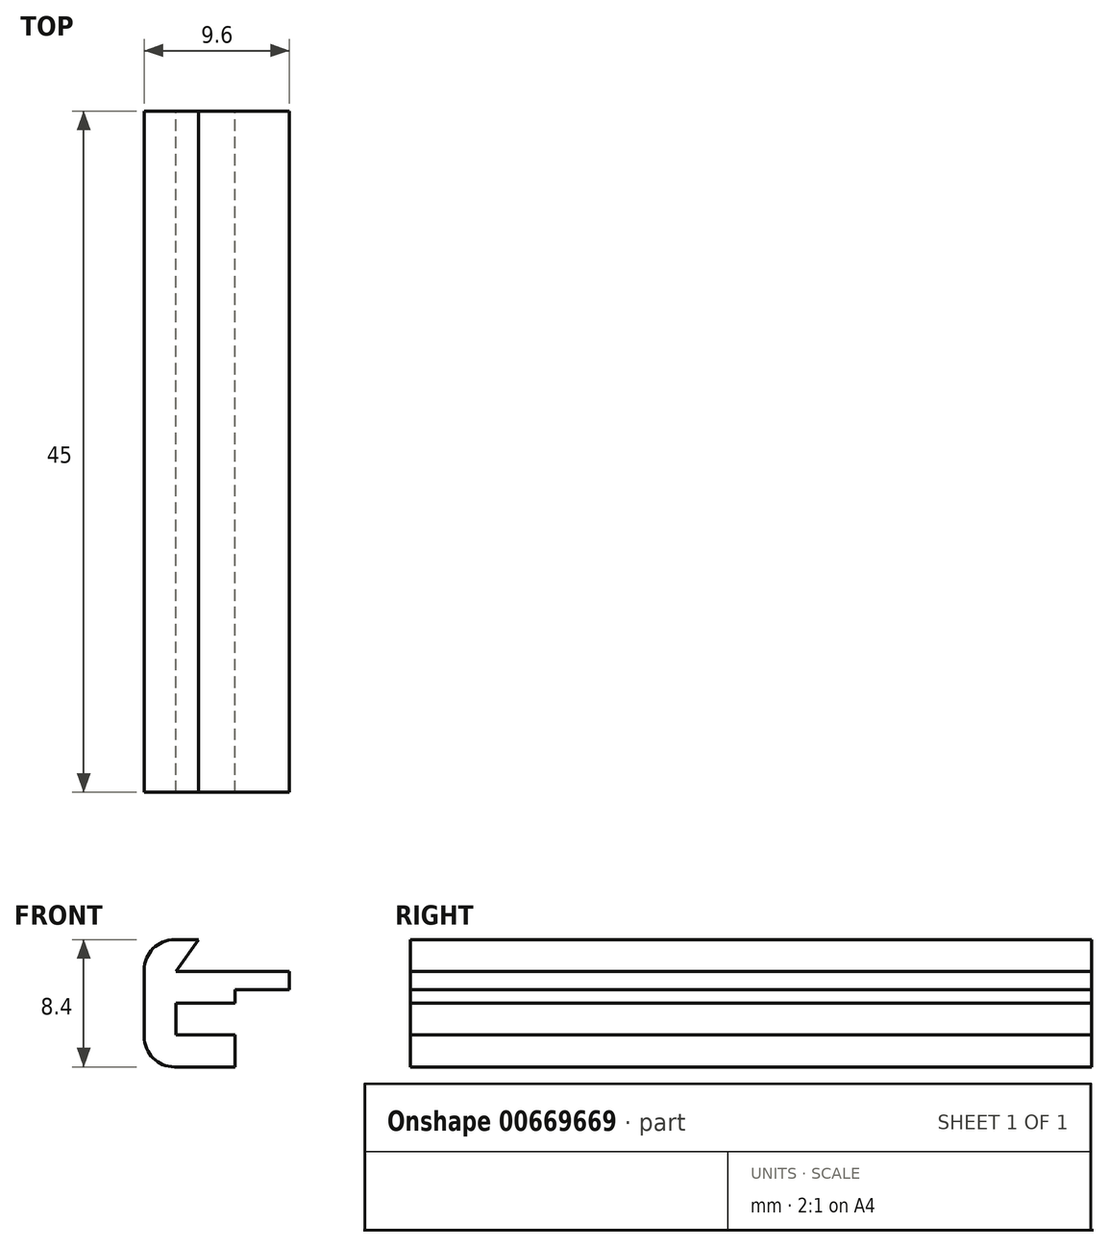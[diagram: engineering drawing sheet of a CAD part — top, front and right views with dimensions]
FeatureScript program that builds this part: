
annotation { "Feature Type Name" : "Feature", "Feature Type Description" : "" }
export const myFeature = defineFeature(function(context is Context, id is Id, definition is map)
    precondition{}
    {
        {
            var Q0;
            Q0=qCreatedBy(makeId("Front.planeOp"),FACE);
            var sketch = newSketch(context, id + "F0", { "sketchPlane" : qUnion([Q0])});
            skLineSegment(sketch, "E0", {"start": v(-2.1, 35.55) * mm, "end": v(-2.1, 27.15) * mm});
            skLineSegment(sketch, "E1", {"start": v(-2.1, 27.15) * mm, "end": v(3.9, 27.15) * mm});
            skLineSegment(sketch, "E2", {"start": v(3.9, 27.15) * mm, "end": v(3.9, 29.25) * mm});
            skLineSegment(sketch, "E3", {"start": v(3.9, 29.25) * mm, "end": v(0, 29.25) * mm});
            skLineSegment(sketch, "E4", {"start": v(0, 29.25) * mm, "end": v(0, 31.35) * mm});
            skLineSegment(sketch, "E5", {"start": v(0, 31.35) * mm, "end": v(3.9, 31.35) * mm});
            skLineSegment(sketch, "E6", {"start": v(3.9, 31.35) * mm, "end": v(3.9, 33.45) * mm});
            skLineSegment(sketch, "E7", {"start": v(3.9, 33.45) * mm, "end": v(0, 33.45) * mm});
            skLineSegment(sketch, "E8", {"start": v(0, 33.45) * mm, "end": v(1.5, 35.55) * mm});
            skLineSegment(sketch, "E9", {"start": v(1.5, 35.55) * mm, "end": v(-2.1, 35.55) * mm});
            skLineSegment(sketch, "E10.bottom", {"start": v(3.9, 33.45) * mm, "end": v(7.5, 33.45) * mm});
            skLineSegment(sketch, "E10.top", {"start": v(3.9, 32.25) * mm, "end": v(7.5, 32.25) * mm});
            skLineSegment(sketch, "E10.left", {"start": v(3.9, 33.45) * mm, "end": v(3.9, 32.25) * mm});
            skLineSegment(sketch, "E10.right", {"start": v(7.5, 33.45) * mm, "end": v(7.5, 32.25) * mm});
            skSolve(sketch);
        }
        {
            var Q0;
            Q0 = qSketchRegion(id + "F0", true);
            extrude(context, id + "F1", {"entities" : qUnion([Q0]), "depth" : 45 * mm, "offsetDistance" : 25 * mm});
        }
        {
            var Q0;
            Q0=makeQuery(id+"F1.opExtrude","SWEPT_EDGE",EDGE,{"disambiguationData":[OSD([sQuery(id+"F0.wireOp",EDGE,"E0"),sQuery(id+"F0.wireOp",EDGE,"E1")])]});
            var Q1;
            Q1=makeQuery(id+"F1.opExtrude","SWEPT_EDGE",EDGE,{"disambiguationData":[OSD([sQuery(id+"F0.wireOp",EDGE,"E0"),sQuery(id+"F0.wireOp",EDGE,"E9")])]});
            fillet(context, id + "F2", {"entities" : qUnion([Q0, Q1]), "radius" : 2 * mm, "tangentPropagation" : true, "allowEdgeOverflow" : false});
        }
    });
